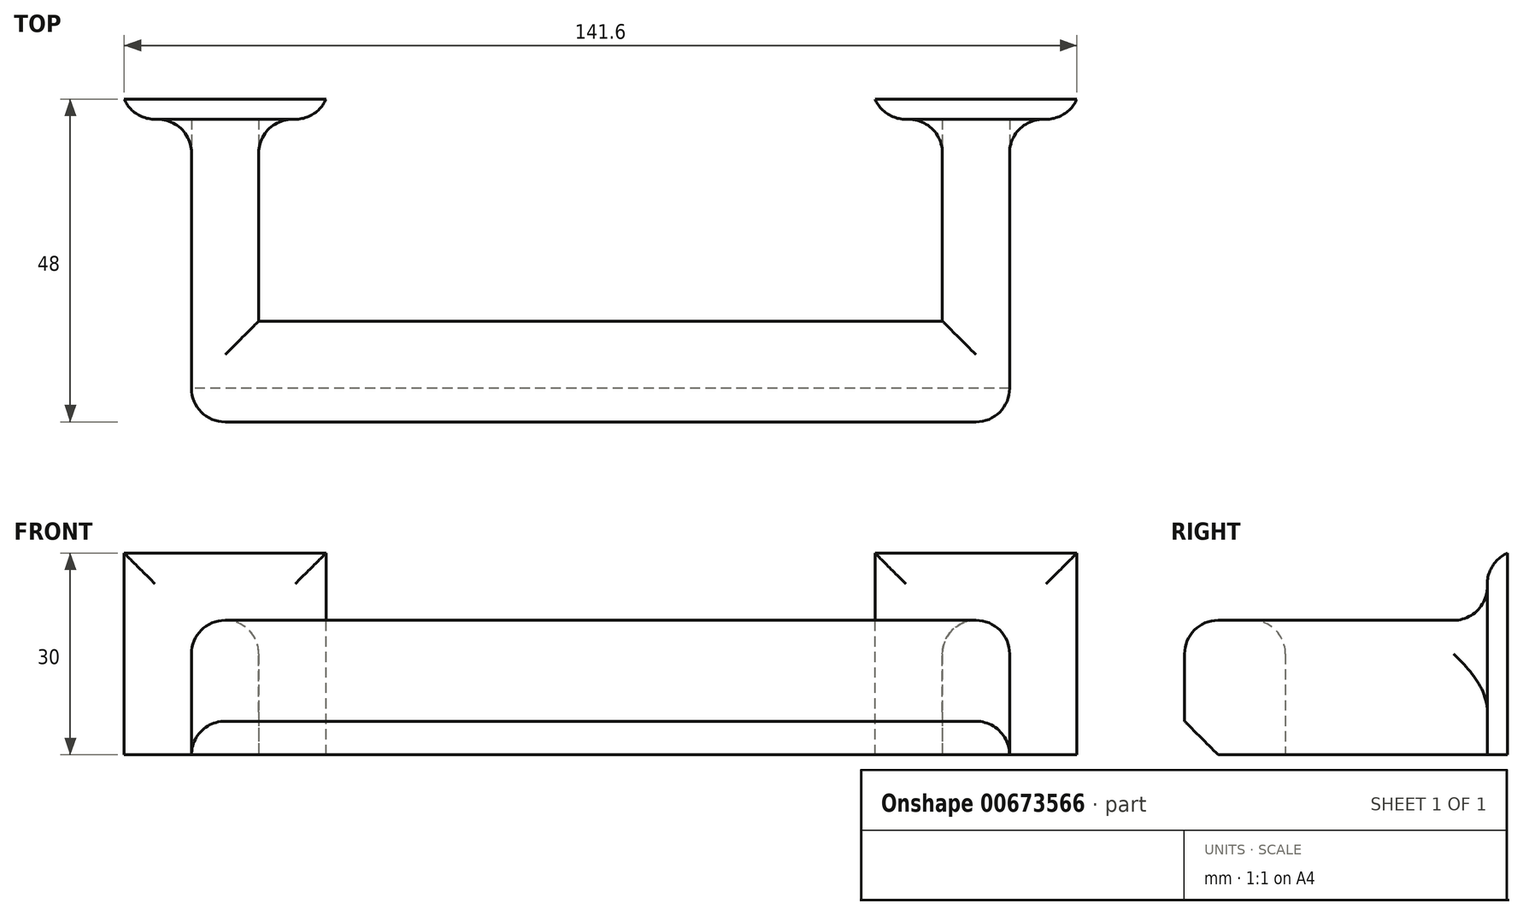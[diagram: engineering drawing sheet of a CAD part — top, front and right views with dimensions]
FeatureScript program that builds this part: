
annotation { "Feature Type Name" : "Feature", "Feature Type Description" : "" }
export const myFeature = defineFeature(function(context is Context, id is Id, definition is map)
    precondition{}
    {
        {
            var Q0;
            Q0=qCreatedBy(makeId("Top.planeOp"),FACE);
            var sketch = newSketch(context, id + "F0", { "sketchPlane" : qUnion([Q0])});
            skLineSegment(sketch, "E0.bottom", {"start": v(50.8, -7.5) * mm, "end": v(-50.8, -7.5) * mm});
            skLineSegment(sketch, "E0.top", {"start": v(50.8, 7.5) * mm, "end": v(-50.8, 7.5) * mm});
            skLineSegment(sketch, "E0.left", {"start": v(50.8, -7.5) * mm, "end": v(50.8, 7.5) * mm});
            skLineSegment(sketch, "E0.right", {"start": v(-50.8, -7.5) * mm, "end": v(-50.8, 7.5) * mm});
            skPoint(sketch, "E0.middle", {"position": v(0, 0) * mm});
            skLineSegment(sketch, "E1.bottom", {"start": v(-50.8, -7.5) * mm, "end": v(-60.8, -7.5) * mm});
            skLineSegment(sketch, "E1.top", {"start": v(-50.8, 37.5) * mm, "end": v(-60.8, 37.5) * mm});
            skLineSegment(sketch, "E1.left", {"start": v(-50.8, -7.5) * mm, "end": v(-50.8, 37.5) * mm});
            skLineSegment(sketch, "E1.right", {"start": v(-60.8, -7.5) * mm, "end": v(-60.8, 37.5) * mm});
            skLineSegment(sketch, "E2.bottom", {"start": v(50.8, -7.5) * mm, "end": v(60.8, -7.5) * mm});
            skLineSegment(sketch, "E2.top", {"start": v(50.8, 37.5) * mm, "end": v(60.8, 37.5) * mm});
            skLineSegment(sketch, "E2.left", {"start": v(50.8, -7.5) * mm, "end": v(50.8, 37.5) * mm});
            skLineSegment(sketch, "E2.right", {"start": v(60.8, -7.5) * mm, "end": v(60.8, 37.5) * mm});
            skPoint(sketch, "E3.middle", {"position": v(-55.8, 37.5) * mm});
            skPoint(sketch, "E4.middle", {"position": v(55.8, 37.5) * mm});
            skSolve(sketch);
        }
        {
            var Q0;
            Q0 = qSketchRegion(id + "F0", true);
            extrude(context, id + "F1", {"entities" : qUnion([Q0]), "depth" : 20 * mm, "offsetDistance" : 25 * mm});
        }
        {
            var Q0;
            Q0=makeQuery(id+"F1.opExtrude","SWEPT_FACE",FACE,{"disambiguationData":[OSD([sQuery(id+"F0.wireOp",EDGE,"E2.top")])]});
            var sketch = newSketch(context, id + "F2", { "sketchPlane" : qUnion([Q0])});
            skLineSegment(sketch, "E5.bottom", {"start": v(-40.8, 0) * mm, "end": v(-70.8, 0) * mm});
            skLineSegment(sketch, "E5.top", {"start": v(-40.8, 30) * mm, "end": v(-70.8, 30) * mm});
            skLineSegment(sketch, "E5.left", {"start": v(-40.8, 0) * mm, "end": v(-40.8, 30) * mm});
            skLineSegment(sketch, "E5.right", {"start": v(-70.8, 0) * mm, "end": v(-70.8, 30) * mm});
            skPoint(sketch, "E5.middle", {"position": v(-55.8, 15) * mm});
            skLineSegment(sketch, "E6.bottom", {"start": v(70.8, 0) * mm, "end": v(40.8, 0) * mm});
            skLineSegment(sketch, "E6.top", {"start": v(70.8, 30) * mm, "end": v(40.8, 30) * mm});
            skLineSegment(sketch, "E6.left", {"start": v(70.8, 0) * mm, "end": v(70.8, 30) * mm});
            skLineSegment(sketch, "E6.right", {"start": v(40.8, 0) * mm, "end": v(40.8, 30) * mm});
            skPoint(sketch, "E6.middle", {"position": v(55.8, 15) * mm});
            skPoint(sketch, "E7", {"position": v(-55.8, 20) * mm});
            skPoint(sketch, "E8", {"position": v(55.8, 20) * mm});
            skSolve(sketch);
        }
        {
            var Q0;
            Q0 = qSketchRegion(id + "F2", true);
            extrude(context, id + "F3", {"entities" : qUnion([Q0]), "operationType" : NewBodyOperationType.ADD, "depth" : 3 * mm, "offsetDistance" : 25 * mm});
        }
        {
            var Q0;
            Q0=makeQuery(id+"F1.opExtrude","CAP_EDGE",EDGE,{"disambiguationData":[OSD([sQuery(id+"F0.wireOp",EDGE,"E1.top")])],"isStart":false});
            var Q1;
            Q1=makeQuery(id+"F1.opExtrude","SWEPT_EDGE",EDGE,{"disambiguationData":[OSD([sQuery(id+"F0.wireOp",EDGE,"E1.top"),sQuery(id+"F0.wireOp",EDGE,"E1.left")])]});
            var Q2;
            Q2=makeQuery(id+"F1.opExtrude","SWEPT_EDGE",EDGE,{"disambiguationData":[OSD([sQuery(id+"F0.wireOp",EDGE,"E1.top"),sQuery(id+"F0.wireOp",EDGE,"E1.right")])]});
            var Q3;
            Q3=makeQuery(id+"F1.opExtrude","SWEPT_EDGE",EDGE,{"disambiguationData":[OSD([sQuery(id+"F0.wireOp",EDGE,"E1.bottom"),sQuery(id+"F0.wireOp",EDGE,"E1.right")])]});
            var Q4;
            Q4=makeQuery(id+"F1.opExtrude","SWEPT_EDGE",EDGE,{"disambiguationData":[OSD([sQuery(id+"F0.wireOp",EDGE,"E2.bottom"),sQuery(id+"F0.wireOp",EDGE,"E2.right")])]});
            var Q5;
            Q5=makeQuery(id+"F1.opExtrude","SWEPT_EDGE",EDGE,{"disambiguationData":[OSD([sQuery(id+"F0.wireOp",EDGE,"E2.top"),sQuery(id+"F0.wireOp",EDGE,"E2.right")])]});
            var Q6;
            Q6=makeQuery(id+"F1.opExtrude","CAP_EDGE",EDGE,{"disambiguationData":[OSD([sQuery(id+"F0.wireOp",EDGE,"E2.top")])],"isStart":false});
            var Q7;
            Q7=makeQuery(id+"F1.opExtrude","SWEPT_EDGE",EDGE,{"disambiguationData":[OSD([sQuery(id+"F0.wireOp",EDGE,"E2.top"),sQuery(id+"F0.wireOp",EDGE,"E2.left")])]});
            var Q8;
            Q8=makeQuery(id+"F1.opExtrude","CAP_FACE",FACE,{"disambiguationData":[OSD([sQuery(id+"F0.wireOp",EDGE,"E0.bottom"),sQuery(id+"F0.wireOp",EDGE,"E0.top"),sQuery(id+"F0.wireOp",EDGE,"E1.bottom"),sQuery(id+"F0.wireOp",EDGE,"E1.top"),sQuery(id+"F0.wireOp",EDGE,"E1.left"),sQuery(id+"F0.wireOp",EDGE,"E1.right"),sQuery(id+"F0.wireOp",EDGE,"E2.bottom"),sQuery(id+"F0.wireOp",EDGE,"E2.top"),sQuery(id+"F0.wireOp",EDGE,"E2.left"),sQuery(id+"F0.wireOp",EDGE,"E2.right")])],"isStart":false});
            fillet(context, id + "F4", {"entities" : qUnion([Q0, Q1, Q2, Q3, Q4, Q5, Q6, Q7, Q8]), "radius" : 5 * mm, "tangentPropagation" : true, "allowEdgeOverflow" : false});
        }
        {
            var Q0;
            Q0=makeQuery(id+"F3.opExtrude","CAP_EDGE",EDGE,{"disambiguationData":[OSD([sQuery(id+"F2.wireOp",EDGE,"E6.top")])],"isStart":true});
            var Q1;
            Q1=makeQuery(id+"F3.opExtrude","CAP_EDGE",EDGE,{"disambiguationData":[OSD([sQuery(id+"F2.wireOp",EDGE,"E6.left")])],"isStart":true});
            var Q2;
            Q2=makeQuery(id+"F3.opExtrude","CAP_EDGE",EDGE,{"disambiguationData":[OSD([sQuery(id+"F2.wireOp",EDGE,"E6.right")])],"isStart":true});
            var Q3;
            Q3=makeQuery(id+"F3.opExtrude","CAP_EDGE",EDGE,{"disambiguationData":[OSD([sQuery(id+"F2.wireOp",EDGE,"E5.left")])],"isStart":true});
            var Q4;
            Q4=makeQuery(id+"F3.opExtrude","CAP_EDGE",EDGE,{"disambiguationData":[OSD([sQuery(id+"F2.wireOp",EDGE,"E5.top")])],"isStart":true});
            var Q5;
            Q5=makeQuery(id+"F3.opExtrude","CAP_EDGE",EDGE,{"disambiguationData":[OSD([sQuery(id+"F2.wireOp",EDGE,"E5.right")])],"isStart":true});
            fillet(context, id + "F5", {"entities" : qUnion([Q0, Q1, Q2, Q3, Q4, Q5]), "radius" : 5 * mm, "tangentPropagation" : true, "allowEdgeOverflow" : false});
        }
        {
            var Q0;
            Q0=makeQuery(id+"F1.opExtrude","CAP_EDGE",EDGE,{"disambiguationData":[OSD([sQuery(id+"F0.wireOp",EDGE,"E0.bottom"),sQuery(id+"F0.wireOp",EDGE,"E1.bottom"),sQuery(id+"F0.wireOp",EDGE,"E2.bottom")])],"isStart":true});
            chamfer(context, id + "F6", {"entities" : qUnion([Q0]), "width" : 5 * mm});
        }
    });
